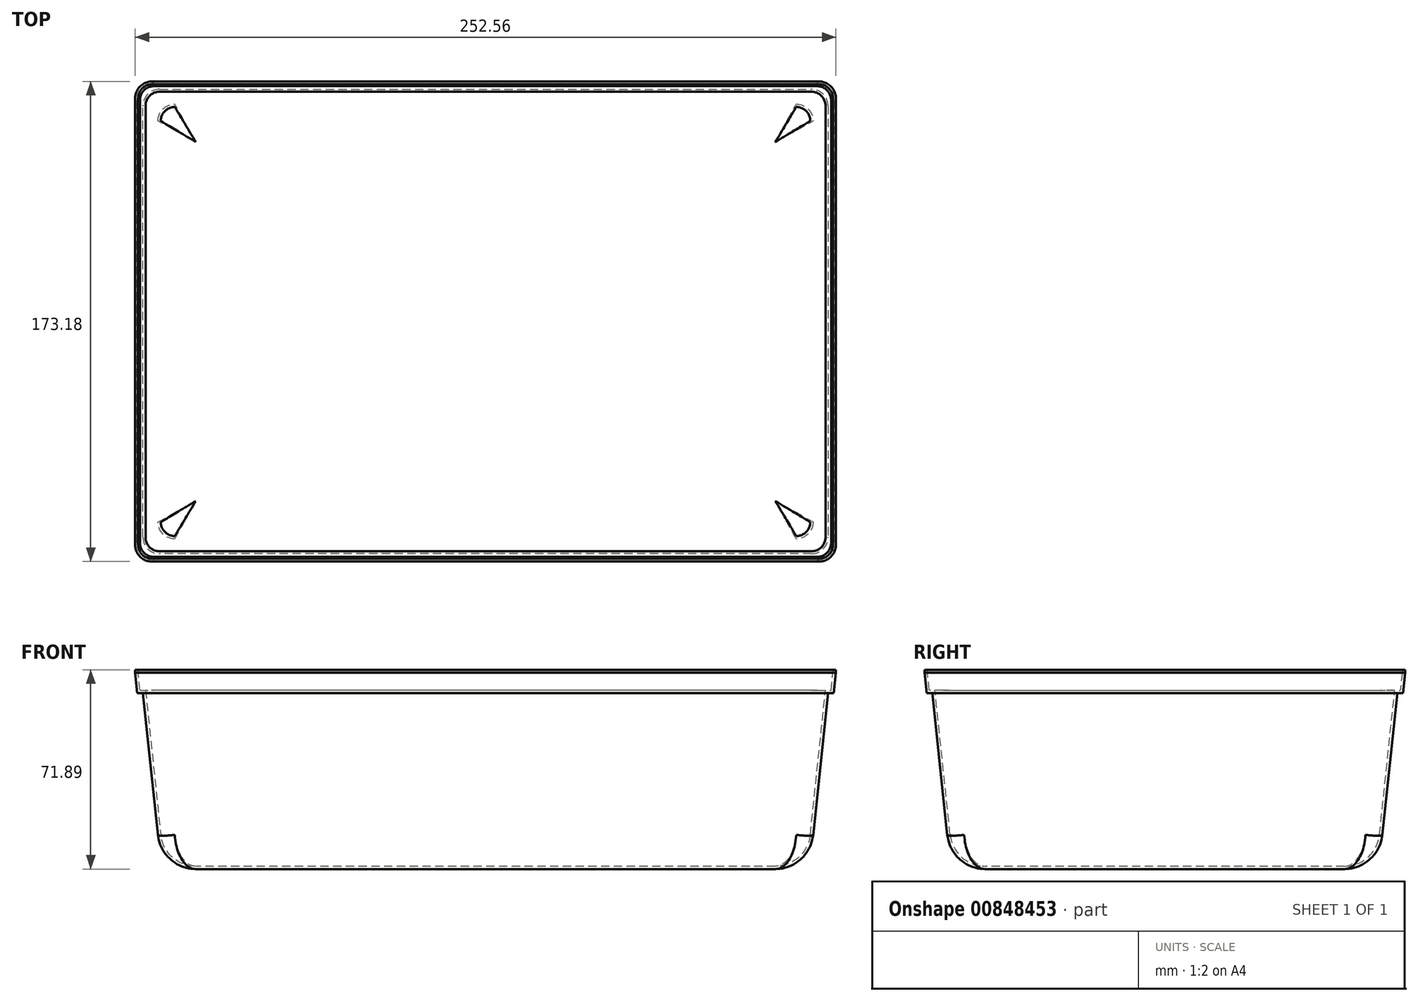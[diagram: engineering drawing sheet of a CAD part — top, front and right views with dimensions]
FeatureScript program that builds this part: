
annotation { "Feature Type Name" : "Feature", "Feature Type Description" : "" }
export const myFeature = defineFeature(function(context is Context, id is Id, definition is map)
    precondition{}
    {
        {
            var Q0;
            Q0=qCreatedBy(makeId("Top.planeOp"),FACE);
            var sketch = newSketch(context, id + "F0", { "sketchPlane" : qUnion([Q0])});
            skLineSegment(sketch, "E0.bottom", {"start": v(-115.89, 76.2) * mm, "end": v(115.89, 76.2) * mm});
            skLineSegment(sketch, "E0.top", {"start": v(-115.89, -76.2) * mm, "end": v(115.89, -76.2) * mm});
            skLineSegment(sketch, "E0.left", {"start": v(-115.89, 76.2) * mm, "end": v(-115.89, -76.2) * mm});
            skLineSegment(sketch, "E0.right", {"start": v(115.89, 76.2) * mm, "end": v(115.89, -76.2) * mm});
            skPoint(sketch, "E0.middle", {"position": v(0, 0) * mm});
            skSolve(sketch);
        }
        {
            var Q0;
            Q0=makeQuery(id+"F0.imprint","IMPRINT",FACE,{"disambiguationData":[TD([[makeQuery(id+"F0.imprint","IMPRINT",EDGE,{"derivedFrom":sQuery(id+"F0.wireOp",EDGE,"E0.bottom")}),-1.0]])]});
            extrude(context, id + "F1", {"entities" : qUnion([Q0]), "depth" : 63.5 * mm, "offsetDistance" : 25.4 * mm, "hasDraft" : true, "draftAngle" : 6 * degree});
        }
        {
            var Q0;
            Q0=makeQuery(id+"F1.opExtrude","CAP_FACE",FACE,{"disambiguationData":[OSD([sQuery(id+"F0.wireOp",EDGE,"E0.bottom"),sQuery(id+"F0.wireOp",EDGE,"E0.top"),sQuery(id+"F0.wireOp",EDGE,"E0.left"),sQuery(id+"F0.wireOp",EDGE,"E0.right")])],"isStart":false});
            var sketch = newSketch(context, id + "F2", { "sketchPlane" : qUnion([Q0])});
            skPoint(sketch, "E1.middle", {"position": v(0, 0) * mm});
            skLineSegment(sketch, "E2.bottom", {"start": v(-124.59, 84.9) * mm, "end": v(124.59, 84.9) * mm});
            skLineSegment(sketch, "E2.top", {"start": v(-124.59, -84.9) * mm, "end": v(124.59, -84.9) * mm});
            skLineSegment(sketch, "E2.left", {"start": v(-124.59, 84.9) * mm, "end": v(-124.59, -84.9) * mm});
            skLineSegment(sketch, "E2.right", {"start": v(124.59, 84.9) * mm, "end": v(124.59, -84.9) * mm});
            skSolve(sketch);
        }
        {
            var Q0;
            Q0=makeQuery(id+"F2.imprint","IMPRINT",FACE,{"disambiguationData":[TD([[makeQuery(id+"F2.imprint","IMPRINT",EDGE,{"derivedFrom":sQuery(id+"F2.wireOp",EDGE,"E2.bottom")}),-1.0]])]});
            var Q1;
            Q1=makeQuery(id+"F2.imprint","IMPRINT",FACE,{"disambiguationData":[TD([[makeQuery(id+"F2.imprint","IMPRINT",EDGE,{"derivedFrom":makeQuery(id+"F1.opExtrude","CAP_EDGE",EDGE,{"disambiguationData":[OSD([sQuery(id+"F0.wireOp",EDGE,"E0.bottom")])],"isStart":false})}),-1.0]])]});
            extrude(context, id + "F3", {"entities" : qUnion([Q0, Q1]), "operationType" : NewBodyOperationType.ADD, "depth" : 6.35 * mm, "offsetDistance" : 25.4 * mm, "hasDraft" : true, "draftAngle" : 6 * degree});
        }
        {
            var Q0;
            Q0=makeQuery(id+"F1.opExtrude","SWEPT_EDGE",EDGE,{"disambiguationData":[OSD([sQuery(id+"F0.wireOp",EDGE,"E0.bottom"),sQuery(id+"F0.wireOp",EDGE,"E0.right")])]});
            var Q1;
            Q1=makeQuery(id+"F1.opExtrude","SWEPT_EDGE",EDGE,{"disambiguationData":[OSD([sQuery(id+"F0.wireOp",EDGE,"E0.bottom"),sQuery(id+"F0.wireOp",EDGE,"E0.left")])]});
            var Q2;
            Q2=makeQuery(id+"F1.opExtrude","SWEPT_EDGE",EDGE,{"disambiguationData":[OSD([sQuery(id+"F0.wireOp",EDGE,"E0.top"),sQuery(id+"F0.wireOp",EDGE,"E0.left")])]});
            var Q3;
            Q3=makeQuery(id+"F1.opExtrude","SWEPT_EDGE",EDGE,{"disambiguationData":[OSD([sQuery(id+"F0.wireOp",EDGE,"E0.top"),sQuery(id+"F0.wireOp",EDGE,"E0.right")])]});
            fillet(context, id + "F4", {"entities" : qUnion([Q0, Q1, Q2, Q3]), "radius" : 5.08 * mm, "tangentPropagation" : true, "allowEdgeOverflow" : false});
        }
        {
            var Q0;
            Q0=makeQuery(id+"F3.opExtrude","SWEPT_EDGE",EDGE,{"disambiguationData":[OSD([sQuery(id+"F2.wireOp",EDGE,"E2.bottom"),sQuery(id+"F2.wireOp",EDGE,"E2.right")])]});
            var Q1;
            Q1=makeQuery(id+"F3.opExtrude","SWEPT_EDGE",EDGE,{"disambiguationData":[OSD([sQuery(id+"F2.wireOp",EDGE,"E2.top"),sQuery(id+"F2.wireOp",EDGE,"E2.right")])]});
            var Q2;
            Q2=makeQuery(id+"F3.opExtrude","SWEPT_EDGE",EDGE,{"disambiguationData":[OSD([sQuery(id+"F2.wireOp",EDGE,"E2.top"),sQuery(id+"F2.wireOp",EDGE,"E2.left")])]});
            var Q3;
            Q3=makeQuery(id+"F3.opExtrude","SWEPT_EDGE",EDGE,{"disambiguationData":[OSD([sQuery(id+"F2.wireOp",EDGE,"E2.bottom"),sQuery(id+"F2.wireOp",EDGE,"E2.left")])]});
            fillet(context, id + "F5", {"entities" : qUnion([Q0, Q1, Q2, Q3]), "radius" : 5.08 * mm, "tangentPropagation" : true, "allowEdgeOverflow" : false});
        }
        {
            var Q0;
            Q0=makeQuery(id+"F1.opExtrude","CAP_EDGE",EDGE,{"disambiguationData":[OSD([sQuery(id+"F0.wireOp",EDGE,"E0.top")])],"isStart":true});
            fillet(context, id + "F6", {"entities" : qUnion([Q0]), "radius" : 12.7 * mm, "tangentPropagation" : true, "allowEdgeOverflow" : false});
        }
        {
            var Q0;
            Q0=makeQuery(id+"F3.opExtrude","CAP_FACE",FACE,{"disambiguationData":[OSD([sQuery(id+"F2.wireOp",EDGE,"E2.bottom"),sQuery(id+"F2.wireOp",EDGE,"E2.top"),sQuery(id+"F2.wireOp",EDGE,"E2.left"),sQuery(id+"F2.wireOp",EDGE,"E2.right")])],"isStart":false});
            shell(context, id + "F7", {"entities" : qUnion([Q0]), "thickness" : 1.02 * mm, "oppositeDirection" : true});
        }
        {
            var Q0;
            Q0=makeQuery(id+"F3.opExtrude","CAP_FACE",FACE,{"disambiguationData":[OSD([sQuery(id+"F2.wireOp",EDGE,"E2.bottom"),sQuery(id+"F2.wireOp",EDGE,"E2.top"),sQuery(id+"F2.wireOp",EDGE,"E2.left"),sQuery(id+"F2.wireOp",EDGE,"E2.right")])],"isStart":false});
            var sketch = newSketch(context, id + "F8", { "sketchPlane" : qUnion([Q0])});
            skLineSegment(sketch, "E3.0", {"start": v(-126.28, 80.53) * mm, "end": v(-126.28, -80.53) * mm});
            skEllipticalArc(sketch, "E3.1", {});
            skLineSegment(sketch, "E3.2", {"start": v(-120.21, 86.59) * mm, "end": v(120.21, 86.59) * mm});
            skEllipticalArc(sketch, "E3.3", {});
            skLineSegment(sketch, "E3.4", {"start": v(126.28, 80.53) * mm, "end": v(126.28, -80.53) * mm});
            skEllipticalArc(sketch, "E3.5", {});
            skLineSegment(sketch, "E3.6", {"start": v(-120.21, -86.59) * mm, "end": v(120.21, -86.59) * mm});
            skEllipticalArc(sketch, "E3.7", {});
            skLineSegment(sketch, "E4.0", {"start": v(-131.61, 80.53) * mm, "end": v(-131.61, -80.53) * mm});
            skFitSpline(sketch, "E4.1", {"points": [v(-112.85, 71.56) * mm, v(-112, 72.32) * mm, v(-111.24, 73.16) * mm, v(-110.35, 74.37) * mm, v(-109.65, 75.7) * mm, v(-109.14, 77.12) * mm, v(-108.78, 78.58) * mm, v(-108.61, 80.46) * mm, v(-108.8, 82.32) * mm, v(-109.18, 83.79) * mm, v(-109.7, 85.2) * mm, v(-110.4, 86.52) * mm, v(-111.3, 87.72) * mm, v(-112.05, 88.56) * mm, v(-112.89, 89.31) * mm, v(-114.09, 90.2) * mm, v(-115.4, 90.92) * mm, v(-116.82, 91.43) * mm, v(-118.28, 91.8) * mm, v(-120.15, 92) * mm, v(-122.02, 91.82) * mm, v(-123.5, 91.46) * mm, v(-124.91, 90.96) * mm, v(-126.24, 90.26) * mm, v(-127.45, 89.36) * mm, v(-128.3, 88.6) * mm, v(-129.05, 87.76) * mm, v(-129.94, 86.55) * mm, v(-130.65, 85.22) * mm, v(-131.15, 83.8) * mm, v(-131.51, 82.34) * mm, v(-131.68, 80.46) * mm, v(-131.5, 78.6) * mm, v(-131.12, 77.13) * mm, v(-130.6, 75.72) * mm, v(-129.9, 74.4) * mm, v(-129, 73.2) * mm, v(-128.24, 72.36) * mm, v(-127.4, 71.6) * mm, v(-126.2, 70.71) * mm, v(-124.89, 70) * mm, v(-123.47, 69.5) * mm, v(-122.01, 69.12) * mm, v(-120.14, 68.92) * mm, v(-118.27, 69.1) * mm, v(-116.8, 69.46) * mm, v(-115.38, 69.96) * mm, v(-114.05, 70.66) * mm, v(-112.85, 71.56) * mm, v(-112, 72.32) * mm, v(-111.24, 73.16) * mm]});
            skFitSpline(sketch, "E4.2", {"points": [v(-111.24, -73.16) * mm, v(-112, -72.32) * mm, v(-112.85, -71.56) * mm, v(-114.05, -70.66) * mm, v(-115.38, -69.96) * mm, v(-116.8, -69.46) * mm, v(-118.27, -69.1) * mm, v(-120.14, -68.92) * mm, v(-122.01, -69.12) * mm, v(-123.47, -69.5) * mm, v(-124.89, -70) * mm, v(-126.2, -70.71) * mm, v(-127.4, -71.6) * mm, v(-128.24, -72.36) * mm, v(-129, -73.2) * mm, v(-129.9, -74.4) * mm, v(-130.6, -75.72) * mm, v(-131.12, -77.13) * mm, v(-131.5, -78.6) * mm, v(-131.68, -80.46) * mm, v(-131.51, -82.34) * mm, v(-131.15, -83.8) * mm, v(-130.65, -85.22) * mm, v(-129.94, -86.55) * mm, v(-129.05, -87.76) * mm, v(-128.3, -88.6) * mm, v(-127.45, -89.36) * mm, v(-126.24, -90.26) * mm, v(-124.91, -90.96) * mm, v(-123.5, -91.46) * mm, v(-122.02, -91.82) * mm, v(-120.15, -92) * mm, v(-118.28, -91.8) * mm, v(-116.82, -91.43) * mm, v(-115.4, -90.92) * mm, v(-114.09, -90.2) * mm, v(-112.89, -89.31) * mm, v(-112.05, -88.56) * mm, v(-111.3, -87.72) * mm, v(-110.4, -86.52) * mm, v(-109.7, -85.2) * mm, v(-109.18, -83.79) * mm, v(-108.8, -82.32) * mm, v(-108.61, -80.46) * mm, v(-108.78, -78.58) * mm, v(-109.14, -77.12) * mm, v(-109.65, -75.7) * mm, v(-110.35, -74.37) * mm, v(-111.24, -73.16) * mm, v(-112, -72.32) * mm, v(-112.85, -71.56) * mm]});
            skLineSegment(sketch, "E4.3", {"start": v(-120.21, 91.92) * mm, "end": v(120.21, 91.92) * mm});
            skLineSegment(sketch, "E4.4", {"start": v(-120.21, -91.92) * mm, "end": v(120.21, -91.92) * mm});
            skFitSpline(sketch, "E4.5", {"points": [v(112.85, -71.56) * mm, v(112, -72.32) * mm, v(111.24, -73.16) * mm, v(110.35, -74.37) * mm, v(109.65, -75.7) * mm, v(109.14, -77.12) * mm, v(108.78, -78.58) * mm, v(108.61, -80.46) * mm, v(108.8, -82.32) * mm, v(109.18, -83.79) * mm, v(109.7, -85.2) * mm, v(110.4, -86.52) * mm, v(111.3, -87.72) * mm, v(112.05, -88.56) * mm, v(112.89, -89.31) * mm, v(114.09, -90.2) * mm, v(115.4, -90.92) * mm, v(116.82, -91.43) * mm, v(118.28, -91.8) * mm, v(120.15, -92) * mm, v(122.02, -91.82) * mm, v(123.5, -91.46) * mm, v(124.91, -90.96) * mm, v(126.24, -90.26) * mm, v(127.45, -89.36) * mm, v(128.3, -88.6) * mm, v(129.05, -87.76) * mm, v(129.94, -86.55) * mm, v(130.65, -85.22) * mm, v(131.15, -83.8) * mm, v(131.51, -82.34) * mm, v(131.68, -80.46) * mm, v(131.5, -78.6) * mm, v(131.12, -77.13) * mm, v(130.6, -75.72) * mm, v(129.9, -74.4) * mm, v(129, -73.2) * mm, v(128.24, -72.36) * mm, v(127.4, -71.6) * mm, v(126.2, -70.71) * mm, v(124.89, -70) * mm, v(123.47, -69.5) * mm, v(122.01, -69.12) * mm, v(120.14, -68.92) * mm, v(118.27, -69.1) * mm, v(116.8, -69.46) * mm, v(115.38, -69.96) * mm, v(114.05, -70.66) * mm, v(112.85, -71.56) * mm, v(112, -72.32) * mm, v(111.24, -73.16) * mm]});
            skLineSegment(sketch, "E4.6", {"start": v(131.61, 80.53) * mm, "end": v(131.61, -80.53) * mm});
            skFitSpline(sketch, "E4.7", {"points": [v(111.24, 73.16) * mm, v(112, 72.32) * mm, v(112.85, 71.56) * mm, v(114.05, 70.66) * mm, v(115.38, 69.96) * mm, v(116.8, 69.46) * mm, v(118.27, 69.1) * mm, v(120.14, 68.92) * mm, v(122.01, 69.12) * mm, v(123.47, 69.5) * mm, v(124.89, 70) * mm, v(126.2, 70.71) * mm, v(127.4, 71.6) * mm, v(128.24, 72.36) * mm, v(129, 73.2) * mm, v(129.9, 74.4) * mm, v(130.6, 75.72) * mm, v(131.12, 77.13) * mm, v(131.5, 78.6) * mm, v(131.68, 80.46) * mm, v(131.51, 82.34) * mm, v(131.15, 83.8) * mm, v(130.65, 85.22) * mm, v(129.94, 86.55) * mm, v(129.05, 87.76) * mm, v(128.3, 88.6) * mm, v(127.45, 89.36) * mm, v(126.24, 90.26) * mm, v(124.91, 90.96) * mm, v(123.5, 91.46) * mm, v(122.02, 91.82) * mm, v(120.15, 92) * mm, v(118.28, 91.8) * mm, v(116.82, 91.43) * mm, v(115.4, 90.92) * mm, v(114.09, 90.2) * mm, v(112.89, 89.31) * mm, v(112.05, 88.56) * mm, v(111.3, 87.72) * mm, v(110.4, 86.52) * mm, v(109.7, 85.2) * mm, v(109.18, 83.79) * mm, v(108.8, 82.32) * mm, v(108.61, 80.46) * mm, v(108.78, 78.58) * mm, v(109.14, 77.12) * mm, v(109.65, 75.7) * mm, v(110.35, 74.37) * mm, v(111.24, 73.16) * mm, v(112, 72.32) * mm, v(112.85, 71.56) * mm]});
            skLineSegment(sketch, "E5.1", {"start": v(-120.2, 85.57) * mm, "end": v(120.2, 85.57) * mm});
            skLineSegment(sketch, "E5.3", {"start": v(125.26, 80.52) * mm, "end": v(125.26, -80.52) * mm});
            skLineSegment(sketch, "E5.5", {"start": v(-120.2, -85.57) * mm, "end": v(120.2, -85.57) * mm});
            skLineSegment(sketch, "E5.7", {"start": v(-125.26, 80.52) * mm, "end": v(-125.26, -80.52) * mm});
            const initialGuessF8  = {"E3.1": [-0.12014745236108829, 0.08045995236108831, 0.7071067811865476, -0.7071067811865476, 0.00616297399752636, 0.006096, 2.361657698713884, 3.921527608465702], "E3.3": [0.12014745236108829, 0.08045995236108833, -0.7071067811865476, -0.7071067811865476, 0.00616297399752636, 0.006096, 2.361657698713882, 3.9215276084657043], "E3.5": [0.12014745236108829, -0.08045995236108833, -0.7071067811865476, 0.7071067811865476, 0.00616297399752636, 0.006096, 2.361657698713884, 3.921527608465702], "E3.7": [-0.12014745236108829, -0.08045995236108833, 0.7071067811865476, 0.7071067811865476, 0.00616297399752636, 0.006096, 2.3616576987138886, 3.9215276084657043], "E3.1": [-0.12014745236108829, 0.08045995236108831, 0.7071067811865476, -0.7071067811865476, 0.0051358116646053, 0.00508, 2.3616576987138846, 3.9215276084657016], "E3.3": [0.12014745236108829, 0.08045995236108833, -0.7071067811865476, -0.7071067811865476, 0.0051358116646053, 0.00508, 2.361657698713882, 3.9215276084657043], "E3.5": [0.12014745236108829, -0.08045995236108833, -0.7071067811865476, 0.7071067811865476, 0.0051358116646053, 0.00508, 2.3616576987138846, 3.9215276084657016], "E3.7": [-0.12014745236108829, -0.08045995236108833, 0.7071067811865476, 0.7071067811865476, 0.0051358116646053, 0.00508, 2.3616576987138846, 3.9215276084657043]};
            skSetInitialGuess(sketch, initialGuessF8);
            skSolve(sketch);
        }
        {
            var Q0;
            Q0=makeQuery(id+"F8.imprint","IMPRINT",FACE,{"disambiguationData":[TD([[makeQuery(id+"F8.imprint","IMPRINT",EDGE,{"derivedFrom":sQuery(id+"F8.wireOp",EDGE,"E3.0")}),-1.0]])]});
            var Q1;
            Q1=makeQuery(id+"F8.imprint","IMPRINT",FACE,{"disambiguationData":[TD([[makeQuery(id+"F8.imprint","IMPRINT",EDGE,{"derivedFrom":sQuery(id+"F8.wireOp",EDGE,"E3.0")}),1.0]])]});
            extrude(context, id + "F9", {"entities" : qUnion([Q0, Q1]), "operationType" : NewBodyOperationType.ADD, "depth" : 1.02 * mm, "offsetDistance" : 25.4 * mm});
        }
    });
